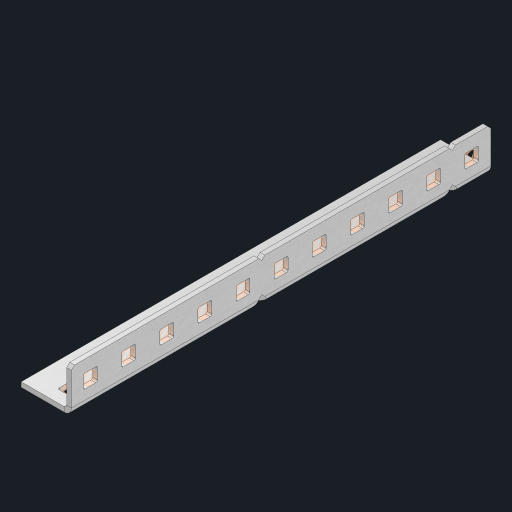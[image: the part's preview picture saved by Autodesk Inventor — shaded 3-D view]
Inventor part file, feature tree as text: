
AUTODESK INVENTOR PART (.ipt)
format: ipt  version: 2023 (Build 270158000, 158)  size: 609,792 bytes
history: native  units: in
note: dims shown in document units (in); Inventor stores cm internally (conversion verified against a paired STEP export)
features: other x27, extrude x21, sheet_metal_op x10, sketch x8, mirror x1, pattern_linear x1, chamfer x1
ambient origin geometry x8: Origin, YZ Plane, XZ Plane, XY Plane, X Axis, Y Axis, Z Axis, Center Point
bodies: Solid1 (feature_tree), Body (feature_tree)
feature tree (69):
  other  "Flange Pattern Plane"
  sheet_metal_op  "Flange Pattern"
  sheet_metal_op  "Body Pattern"
  other  "Arc Length"
  mirror  "Notch Mirror"
  pattern_linear  "Notch Pattern"  Spacing1=0.25in  [1 undecoded]
  chamfer  "End Chamfer"
  extrude  "Half Cut"  Depth=0.0625in
  sketch  "Sketch1"  dims[d0=1.5in]
  other  "Plate1"
  sketch  "Sketch2"  dims[d1=5.5in]
  other  "Plate2"
  sheet_metal_op  "Bend1"
  sheet_metal_op  "Corner1"
  sketch  "Sketch3"  dims[d2=0.0625in]
  other  "Flange Pattern Sketch"
  sketch  "Sketch7"  dims[d3=0.0625in]
  other  "Srf1"
  other  "Srf2"
  sketch  "Sketch8"  dims[d4=0.0312in]
  sketch  "Sketch9"  dims[d5=0.125in]
  other  "Srf91"
  sheet_metal_op  "Body Pattern Sketch"
  other  "Srf92"
  sketch  "Sketch13"  dims[d6=0.0625in]
  sketch  "Sketch14"  dims[d7=0.5in d8=90.0deg d9=0.0312in d10=0.25in d11=0.0625in d12=0.0625in d16=0.182in d17=0.02in d18=0.0625in d19=0.0in d20=0.25in d21=0.25in d46=0.172in d47=1.0in d48=0.0in d49=0.182in d50=0.02in d51=0.25in d52=0.25in d53=0.0625in d54=0.0in d55=0.172in d56=1.0in d57=0.0in d60=4.3307in d62=0.5in d63=0.3937in d65=0.5in d85=0.1473in d86=0.1782in d88=0.04in d89=0.0625in d90=0.0in d91=0.04in d92=0.0491in d95=2.5in d96=0.04in d97=0.25in d98=45.0deg d101=0.0in d102=2.497in d131=0.5in d132=4.3307in d134=0.5in d139=0.5in]
  other  "Srf856"
  other  "Srf1310"
  other  "Srf1311"
  other  "Srf1312"
  other  "Srf1376"
  other  "Srf1377"
  other  "Srf1728"
  other  "Srf1755"
  other  "Srf1878"
  other  "Srf1879"
  other  "Srf1880"
  other  "Srf1881"
  other  "Srf1882"
  other  "Srf1942"
  other  "Srf1943"
  other  "Srf1944"
  other  "Srf1945"
  other  "Srf1946"
  sheet_metal_op  "Flange Stamp"
  sheet_metal_op  "Flange Circle"
  sheet_metal_op  "Body Stamp"
  sheet_metal_op  "Body Circle"
  sheet_metal_op  "Notch"
  extrude  "ExtrusionSrf2"  Depth=0.0625in
  extrude  "ExtrusionSrf92"  Depth=0.5in
  extrude  "ExtrusionSrf856"  Depth=0.02in
  extrude  "ExtrusionSrf1310"  Depth=0.0625in
  extrude  "ExtrusionSrf1311"  TaperAngle=0.0deg  [1 undecoded]
  extrude  "ExtrusionSrf1312"  Depth=0.5in
  extrude  "ExtrusionSrf1376"  Depth=0.5in
  extrude  "ExtrusionSrf1377"  Depth=0.5in
  extrude  "ExtrusionSrf1728"  Depth=0.5in TaperAngle=0.0deg
  extrude  "ExtrusionSrf1755"  Depth=0.5in
  extrude  "ExtrusionSrf1878"  Depth=0.02in
  extrude  "ExtrusionSrf1879"  Depth=0.5in
  extrude  "ExtrusionSrf1880"  Depth=0.5in
  extrude  "ExtrusionSrf1881"  Depth=0.0625in
  extrude  "ExtrusionSrf1882"  TaperAngle=0.0deg  [1 undecoded]
  extrude  "ExtrusionSrf1942"  Depth=0.5in
  extrude  "ExtrusionSrf1943"  Depth=0.5in TaperAngle=0.0deg
  extrude  "ExtrusionSrf1944"  Depth=0.5in
  extrude  "ExtrusionSrf1945"  Depth=0.5in
  extrude  "ExtrusionSrf1946"  Depth=0.5in
note: 3 required parameter values undecoded (feature->parameter linkage not recoverable at this tier; creation-order binding heuristic only, values carry confidence <= 0.55)
